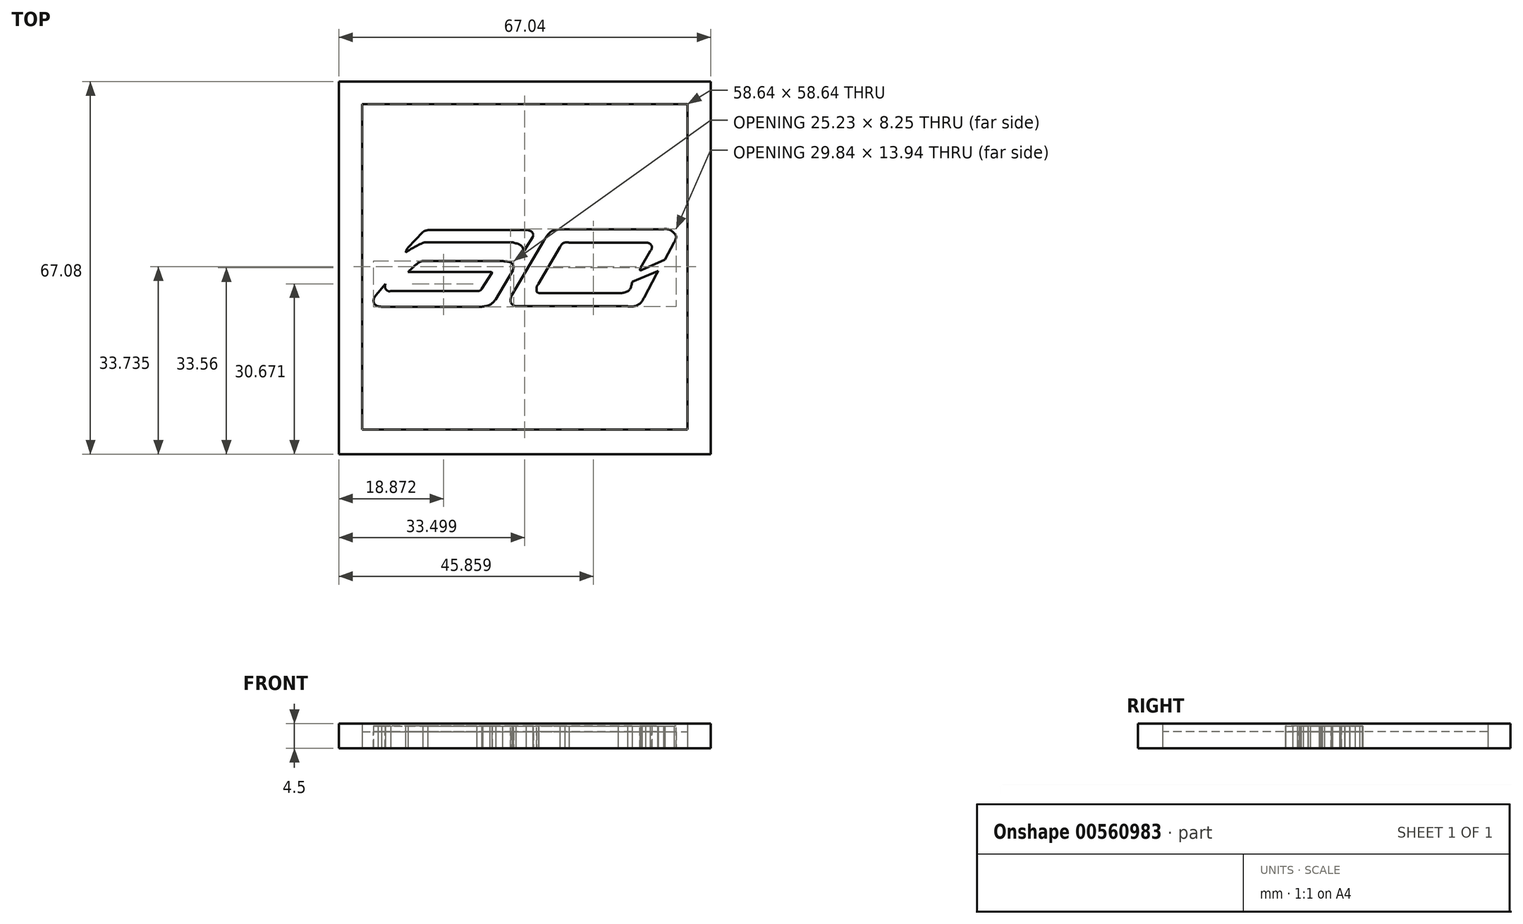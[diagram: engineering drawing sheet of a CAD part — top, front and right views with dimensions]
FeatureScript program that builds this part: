
annotation { "Feature Type Name" : "Feature", "Feature Type Description" : "" }
export const myFeature = defineFeature(function(context is Context, id is Id, definition is map)
    precondition{}
    {
        {
            var Q0;
            Q0=qCreatedBy(makeId("Top.planeOp"),FACE);
            var sketch = newSketch(context, id + "F0", { "sketchPlane" : qUnion([Q0])});
            skLineSegment(sketch, "E0", {"start": v(-6.42, 13) * mm, "end": v(7.53, 13) * mm});
            skLineSegment(sketch, "E1", {"start": v(5.65, 10.83) * mm, "end": v(3.8, 7.97) * mm});
            skLineSegment(sketch, "E2", {"start": v(2.9, 7.57) * mm, "end": v(-12.6, 7.57) * mm});
            skLineSegment(sketch, "E3", {"start": v(-14.27, 4.75) * mm, "end": v(3.8, 4.75) * mm});
            skLineSegment(sketch, "E4", {"start": v(3.8, 4.75) * mm, "end": v(4.01, 4.77) * mm});
            skLineSegment(sketch, "E5", {"start": v(9.43, 11.35) * mm, "end": v(6.31, 6.06) * mm});
            skLineSegment(sketch, "E6", {"start": v(-6.8, 18.16) * mm, "end": v(-9.45, 15.41) * mm});
            skLineSegment(sketch, "E7", {"start": v(-5.37, 18.59) * mm, "end": v(11.8, 18.59) * mm});
            skLineSegment(sketch, "E8", {"start": v(13.02, 17.28) * mm, "end": v(11.8, 15.41) * mm});
            skLineSegment(sketch, "E9", {"start": v(9.42, 16.32) * mm, "end": v(-5.94, 16.32) * mm});
            skLineSegment(sketch, "E10", {"start": v(5.23, 11.01) * mm, "end": v(-9.45, 11.01) * mm});
            skFitSpline(sketch, "E11", {"points": [v(-6.8, 18.16) * mm, v(-6.5, 18.38) * mm, v(-5.76, 18.57) * mm, v(-5.37, 18.59) * mm], "startDerivative": vector(0.81, 0.82) * mm, "endDerivative": vector(1.16, 0) * mm});
            skFitSpline(sketch, "E12", {"points": [v(-5.94, 16.32) * mm, v(-6.51, 16.32) * mm, v(-8.76, 15.24) * mm, v(-9.9, 14.51) * mm], "startDerivative": vector(-2.13, 0.44) * mm, "endDerivative": vector(-2.85, -1.97) * mm});
            skFitSpline(sketch, "E13", {"points": [v(-9.9, 14.51) * mm, v(-9.7, 15.06) * mm, v(-9.45, 15.41) * mm], "startDerivative": vector(0.33, 1.09) * mm, "endDerivative": vector(0.56, 0.7) * mm});
            skFitSpline(sketch, "E14", {"points": [v(-6.42, 13) * mm, v(-7.24, 12.85) * mm, v(-9.45, 11.01) * mm], "startDerivative": vector(-2.15, 0.02) * mm, "endDerivative": vector(-3.75, -3.61) * mm});
            skFitSpline(sketch, "E15", {"points": [v(2.9, 7.57) * mm, v(3.22, 7.57) * mm, v(3.65, 7.75) * mm, v(3.8, 7.97) * mm], "startDerivative": vector(0.9, -0.1) * mm, "endDerivative": vector(0.36, 0.77) * mm});
            skFitSpline(sketch, "E16", {"points": [v(4.01, 4.77) * mm, v(5, 4.99) * mm, v(5.8, 5.47) * mm, v(6.31, 6.06) * mm], "startDerivative": vector(2.88, 0.43) * mm, "endDerivative": vector(1.5, 2) * mm});
            skFitSpline(sketch, "E17", {"points": [v(-12.6, 7.57) * mm, v(-13.05, 7.57) * mm, v(-13.53, 8.04) * mm, v(-13.56, 8.85) * mm], "startDerivative": vector(-1.58, -0.29) * mm, "endDerivative": vector(0.3, 2.26) * mm});
            skLineSegment(sketch, "E18", {"start": v(-13.56, 8.85) * mm, "end": v(-14.9, 7.3) * mm});
            skFitSpline(sketch, "E19", {"points": [v(-14.9, 7.3) * mm, v(-15.63, 6.18) * mm, v(-15.6, 5.44) * mm, v(-15.11, 4.92) * mm, v(-14.27, 4.75) * mm], "startDerivative": vector(-2.99, -3.71) * mm, "endDerivative": vector(3.66, -0.32) * mm});
            skFitSpline(sketch, "E20", {"points": [v(7.53, 13) * mm, v(8.7, 12.85) * mm, v(9.32, 12.5) * mm, v(9.55, 11.98) * mm, v(9.43, 11.35) * mm], "startDerivative": vector(3.4, -0.77) * mm, "endDerivative": vector(-0.83, -2.74) * mm});
            skFitSpline(sketch, "E21", {"points": [v(5.23, 11.01) * mm, v(5.47, 10.99) * mm, v(5.67, 10.92) * mm, v(5.65, 10.83) * mm], "startDerivative": vector(0.58, -0.06) * mm, "endDerivative": vector(-0.2, -0.41) * mm});
            skFitSpline(sketch, "E22", {"points": [v(9.42, 16.32) * mm, v(10.63, 15.93) * mm, v(11.26, 15.28) * mm, v(11.46, 14.8) * mm, v(11.8, 15.41) * mm], "startDerivative": vector(4.2, -0.99) * mm, "endDerivative": vector(1.71, 4.05) * mm});
            skFitSpline(sketch, "E23", {"points": [v(11.8, 18.59) * mm, v(12.59, 18.38) * mm, v(13.08, 17.83) * mm, v(13.02, 17.28) * mm], "startDerivative": vector(2.3, -0.3) * mm, "endDerivative": vector(-0.6, -1.86) * mm});
            skLineSegment(sketch, "E24", {"start": v(18.76, 18.72) * mm, "end": v(36.54, 18.72) * mm});
            skLineSegment(sketch, "E25", {"start": v(19.55, 16.3) * mm, "end": v(33.34, 16.3) * mm});
            skLineSegment(sketch, "E26", {"start": v(32.69, 11.4) * mm, "end": v(36.82, 13.26) * mm});
            skLineSegment(sketch, "E27", {"start": v(36.82, 13.26) * mm, "end": v(38.49, 16.32) * mm});
            skLineSegment(sketch, "E28", {"start": v(34.17, 14.76) * mm, "end": v(32.45, 11.78) * mm});
            skLineSegment(sketch, "E29", {"start": v(30.92, 9.24) * mm, "end": v(35.3, 11.09) * mm});
            skLineSegment(sketch, "E30", {"start": v(35.3, 10.64) * mm, "end": v(33.05, 6.37) * mm});
            skLineSegment(sketch, "E31", {"start": v(17.91, 15.45) * mm, "end": v(14, 8.82) * mm});
            skLineSegment(sketch, "E32", {"start": v(28.4, 7.22) * mm, "end": v(14.1, 7.22) * mm});
            skLineSegment(sketch, "E33", {"start": v(15, 16.62) * mm, "end": v(9.24, 6.87) * mm});
            skLineSegment(sketch, "E34", {"start": v(9.93, 4.82) * mm, "end": v(30.07, 4.82) * mm});
            skFitSpline(sketch, "E35", {"points": [v(15, 16.62) * mm, v(15.54, 17.48) * mm, v(16.55, 18.43) * mm, v(18.76, 18.72) * mm], "startDerivative": vector(1.77, 2.98) * mm, "endDerivative": vector(5.56, 0.12) * mm});
            skFitSpline(sketch, "E36", {"points": [v(17.91, 15.45) * mm, v(18.3, 16.08) * mm, v(18.76, 16.3) * mm, v(19.55, 16.3) * mm], "startDerivative": vector(1.23, 2) * mm, "endDerivative": vector(2.93, -0.27) * mm});
            skFitSpline(sketch, "E37", {"points": [v(33.34, 16.3) * mm, v(33.88, 16.22) * mm, v(34.3, 15.93) * mm, v(34.5, 15.44) * mm, v(34.17, 14.76) * mm], "startDerivative": vector(2.29, -0.2) * mm, "endDerivative": vector(-1.69, -2.41) * mm});
            skFitSpline(sketch, "E38", {"points": [v(36.54, 18.72) * mm, v(37.58, 18.65) * mm, v(38.37, 18.12) * mm, v(38.83, 17.41) * mm, v(38.49, 16.32) * mm], "startDerivative": vector(4.25, 0.18) * mm, "endDerivative": vector(-2.14, -4.34) * mm});
            skFitSpline(sketch, "E39", {"points": [v(30.07, 4.82) * mm, v(31.16, 4.82) * mm, v(32.33, 5.35) * mm, v(33.05, 6.37) * mm], "startDerivative": vector(3.38, -0.3) * mm, "endDerivative": vector(1.78, 3.3) * mm});
            skLineSegment(sketch, "E40", {"start": v(35.3, 11.09) * mm, "end": v(35.47, 11.16) * mm});
            skLineSegment(sketch, "E41", {"start": v(35.3, 10.64) * mm, "end": v(35.62, 11.21) * mm});
            skLineSegment(sketch, "E42", {"start": v(35.47, 11.16) * mm, "end": v(35.62, 11.21) * mm});
            skFitSpline(sketch, "E43", {"points": [v(32.69, 11.4) * mm, v(32.48, 11.3) * mm, v(32.31, 11.37) * mm, v(32.45, 11.78) * mm], "startDerivative": vector(-0.65, -0.43) * mm, "endDerivative": vector(0.62, 1.17) * mm});
            skFitSpline(sketch, "E44", {"points": [v(14, 8.82) * mm, v(13.71, 8.3) * mm, v(13.67, 7.85) * mm, v(13.75, 7.41) * mm, v(14.1, 7.22) * mm], "startDerivative": vector(-1.2, -1.9) * mm, "endDerivative": vector(1.82, -0.56) * mm});
            skFitSpline(sketch, "E45", {"points": [v(9.93, 4.82) * mm, v(9.5, 5.05) * mm, v(9.12, 5.38) * mm, v(9, 6.06) * mm, v(9.24, 6.87) * mm], "startDerivative": vector(-1.93, 1) * mm, "endDerivative": vector(1.01, 2.75) * mm});
            skFitSpline(sketch, "E46", {"points": [v(30.92, 9.24) * mm, v(30.7, 8.34) * mm, v(30.32, 7.71) * mm, v(29.42, 7.28) * mm, v(28.4, 7.22) * mm], "startDerivative": vector(-0.77, -3.76) * mm, "endDerivative": vector(-3.87, 0.12) * mm});
            skLineSegment(sketch, "E47", {"start": v(-17.76, 41.25) * mm, "end": v(40.88, 41.25) * mm});
            skLineSegment(sketch, "E48", {"start": v(40.88, -17.39) * mm, "end": v(-17.76, -17.39) * mm});
            skLineSegment(sketch, "E49", {"start": v(-17.76, 41.25) * mm, "end": v(-17.76, -17.39) * mm});
            skLineSegment(sketch, "E50", {"start": v(-17.76, -17.39) * mm, "end": v(40.88, -17.39) * mm});
            skLineSegment(sketch, "E51", {"start": v(40.88, 41.25) * mm, "end": v(40.88, -17.39) * mm});
            skLineSegment(sketch, "E52.bottom", {"start": v(-21.94, 45.28) * mm, "end": v(45.1, 45.28) * mm});
            skLineSegment(sketch, "E52.top", {"start": v(-21.94, -21.8) * mm, "end": v(45.1, -21.8) * mm});
            skLineSegment(sketch, "E52.left", {"start": v(-21.94, 45.28) * mm, "end": v(-21.94, -21.8) * mm});
            skLineSegment(sketch, "E52.right", {"start": v(45.1, 45.28) * mm, "end": v(45.1, -21.8) * mm});
            skSolve(sketch);
        }
        {
            var Q0;
            Q0=makeQuery(id+"F0.imprint","IMPRINT",FACE,{"disambiguationData":[TD([[makeQuery(id+"F0.imprint","IMPRINT",EDGE,{"derivedFrom":sQuery(id+"F0.wireOp",EDGE,"E0")}),-1.0]])]});
            var Q1;
            Q1=makeQuery(id+"F0.imprint","IMPRINT",FACE,{"disambiguationData":[TD([[makeQuery(id+"F0.imprint","IMPRINT",EDGE,{"derivedFrom":sQuery(id+"F0.wireOp",EDGE,"E6")}),1.0]])]});
            var Q2;
            Q2=makeQuery(id+"F0.imprint","IMPRINT",FACE,{"disambiguationData":[TD([[makeQuery(id+"F0.imprint","IMPRINT",EDGE,{"derivedFrom":sQuery(id+"F0.wireOp",EDGE,"E24")}),-1.0]])]});
            extrude(context, id + "F1", {"entities" : qUnion([Q0, Q1, Q2]), "depth" : 4 * mm, "offsetDistance" : 25 * mm});
        }
        {
            var Q0;
            Q0=makeQuery(id+"F0.imprint","IMPRINT",FACE,{"disambiguationData":[TD([[makeQuery(id+"F0.imprint","IMPRINT",EDGE,{"derivedFrom":sQuery(id+"F0.wireOp",EDGE,"E47")}),1.0]])]});
            extrude(context, id + "F2", {"entities" : qUnion([Q0]), "depth" : 4.5 * mm, "offsetDistance" : 25 * mm});
        }
        {
            var Q0;
            Q0=makeQuery(id+"F0.imprint","IMPRINT",FACE,{"disambiguationData":[TD([[makeQuery(id+"F0.imprint","IMPRINT",EDGE,{"derivedFrom":sQuery(id+"F0.wireOp",EDGE,"E0")}),1.0]])]});
            extrude(context, id + "F3", {"entities" : qUnion([Q0]), "depth" : 3 * mm, "offsetDistance" : 25 * mm});
        }
    });
